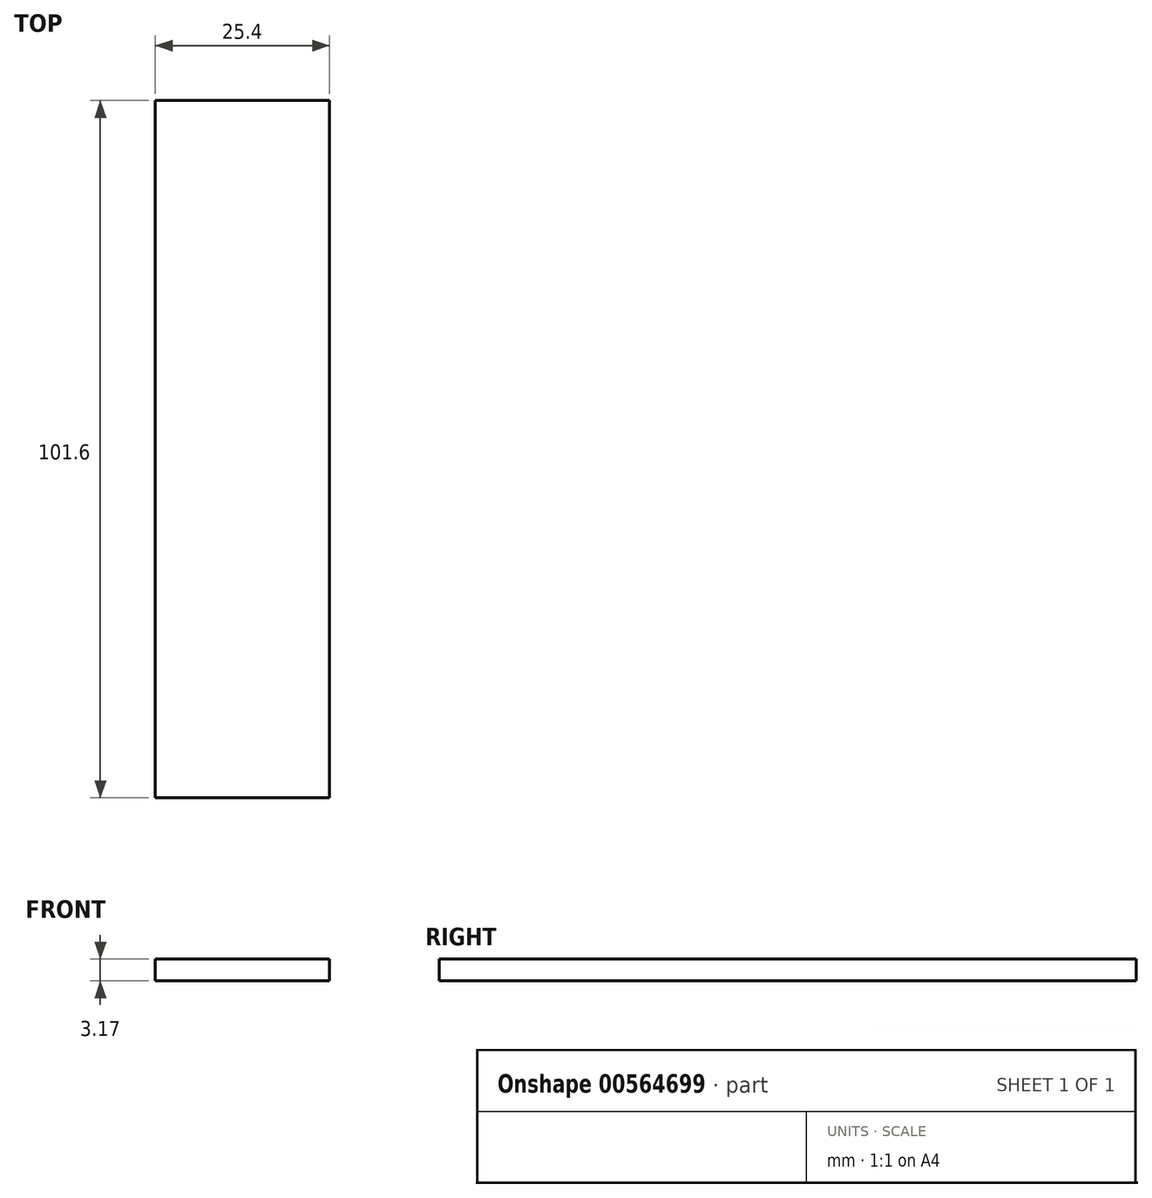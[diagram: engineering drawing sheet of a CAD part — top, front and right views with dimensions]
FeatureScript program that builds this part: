
annotation { "Feature Type Name" : "Feature", "Feature Type Description" : "" }
export const myFeature = defineFeature(function(context is Context, id is Id, definition is map)
    precondition{}
    {
        {
            var Q0;
            Q0=qCreatedBy(makeId("Front.planeOp"),FACE);
            var sketch = newSketch(context, id + "F0", { "sketchPlane" : qUnion([Q0])});
            skLineSegment(sketch, "E0.bottom", {"start": v(0, 0) * mm, "end": v(25.4, 0) * mm});
            skLineSegment(sketch, "E0.top", {"start": v(0, 3.18) * mm, "end": v(25.4, 3.18) * mm});
            skLineSegment(sketch, "E0.left", {"start": v(0, 0) * mm, "end": v(0, 3.18) * mm});
            skLineSegment(sketch, "E0.right", {"start": v(25.4, 0) * mm, "end": v(25.4, 3.18) * mm});
            skSolve(sketch);
        }
        {
            var Q0;
            Q0=makeQuery(id+"F0.imprint","IMPRINT",FACE,{"disambiguationData":[TD([[makeQuery(id+"F0.imprint","IMPRINT",EDGE,{"derivedFrom":sQuery(id+"F0.wireOp",EDGE,"E0.bottom")}),1.0]])]});
            extrude(context, id + "F1", {"entities" : qUnion([Q0]), "depth" : 101.6 * mm, "offsetDistance" : 25.4 * mm});
        }
    });
